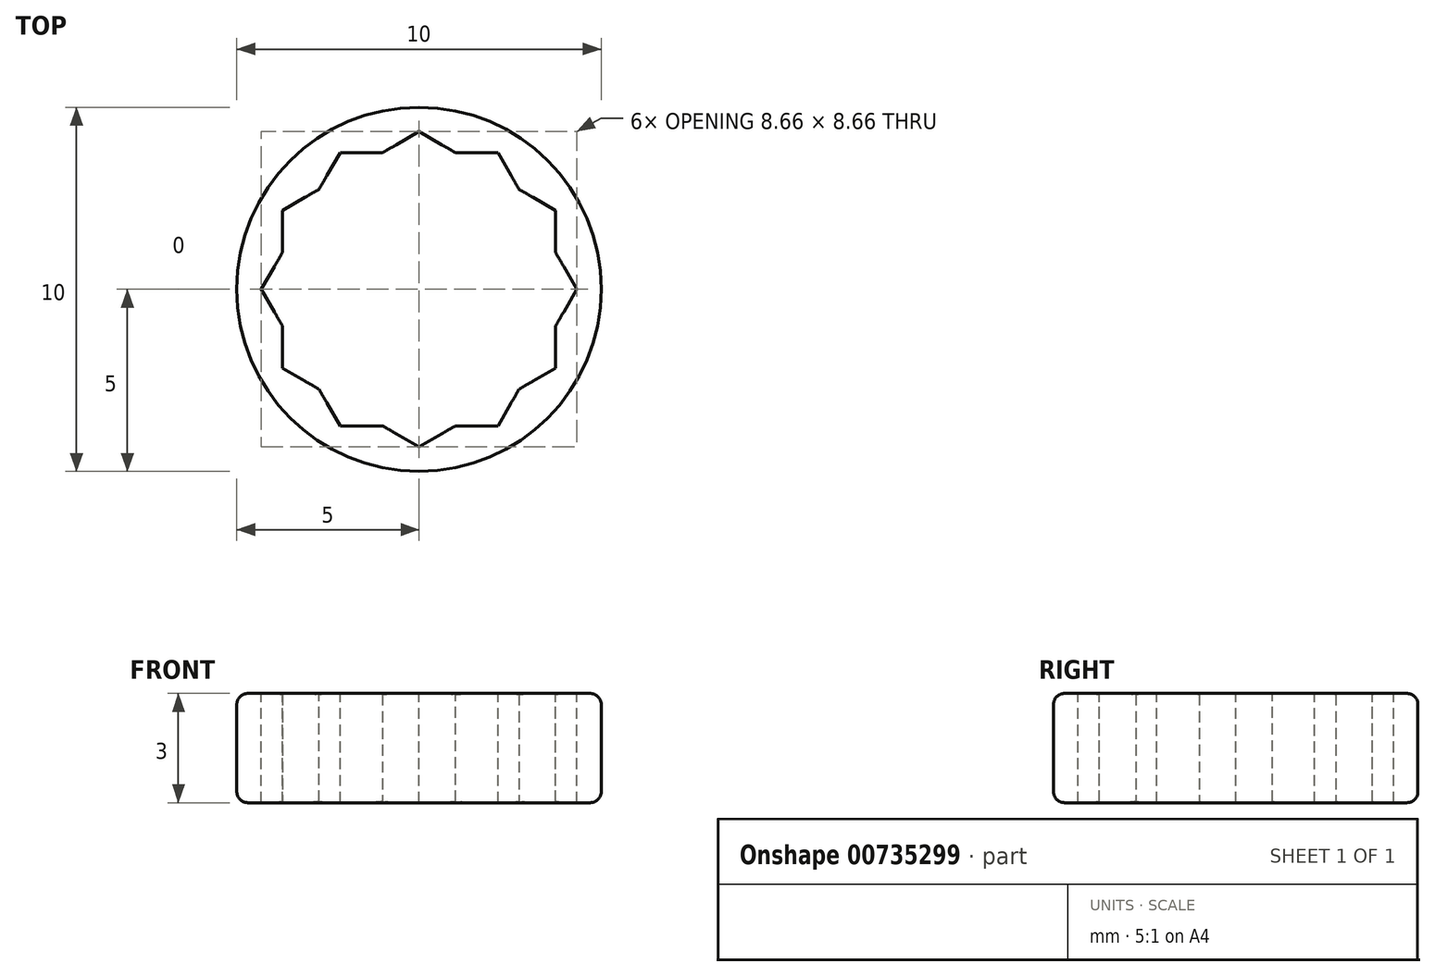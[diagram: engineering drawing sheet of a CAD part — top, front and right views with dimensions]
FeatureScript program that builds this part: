
annotation { "Feature Type Name" : "Feature", "Feature Type Description" : "" }
export const myFeature = defineFeature(function(context is Context, id is Id, definition is map)
    precondition{}
    {
        {
            var Q0;
            Q0=qCreatedBy(makeId("Top.planeOp"),FACE);
            var sketch = newSketch(context, id + "F0", { "sketchPlane" : qUnion([Q0])});
            skCircle(sketch, "E0", {"center": v(0, 0) * mm, "radius": 5 * mm});
            skCircle(sketch, "E1", {"center": v(0, 0) * mm, "radius": 3.72 * mm});
            skSolve(sketch);
        }
        {
            var Q0;
            Q0=makeQuery(id+"F0.imprint","IMPRINT",FACE,{"disambiguationData":[TD([[makeQuery(id+"F0.imprint","IMPRINT",EDGE,{"derivedFrom":sQuery(id+"F0.wireOp",EDGE,"E0")}),1.0]])]});
            extrude(context, id + "F1", {"entities" : qUnion([Q0]), "depth" : 3 * mm, "offsetDistance" : 25 * mm});
        }
        {
            var Q0;
            Q0=makeQuery(id+"F1.opExtrude","CAP_EDGE",EDGE,{"disambiguationData":[OSD([sQuery(id+"F0.wireOp",EDGE,"E0")])],"isStart":false});
            var Q1;
            Q1=makeQuery(id+"F1.opExtrude","CAP_EDGE",EDGE,{"disambiguationData":[OSD([sQuery(id+"F0.wireOp",EDGE,"E1")])],"isStart":false});
            var Q2;
            Q2=makeQuery(id+"F1.opExtrude","CAP_EDGE",EDGE,{"disambiguationData":[OSD([sQuery(id+"F0.wireOp",EDGE,"E0")])],"isStart":true});
            var Q3;
            Q3=makeQuery(id+"F1.opExtrude","CAP_EDGE",EDGE,{"disambiguationData":[OSD([sQuery(id+"F0.wireOp",EDGE,"E1")])],"isStart":true});
            fillet(context, id + "F2", {"entities" : qUnion([Q0, Q1, Q2, Q3]), "radius" : 0.3 * mm, "tangentPropagation" : true, "allowEdgeOverflow" : false});
        }
        {
            var Q0;
            Q0=qCreatedBy(makeId("Top.planeOp"),FACE);
            var sketch = newSketch(context, id + "F3", { "sketchPlane" : qUnion([Q0])});
            skCircle(sketch, "E2.cCircle", {"center": v(0, 0) * mm, "radius": 3.75 * mm, "construction": true});
            skLineSegment(sketch, "E2.0", {"start": v(3.75, 2.17) * mm, "end": v(3.75, -2.17) * mm});
            skLineSegment(sketch, "E2.1", {"start": v(3.75, -2.17) * mm, "end": v(0, -4.33) * mm});
            skLineSegment(sketch, "E2.2", {"start": v(0, -4.33) * mm, "end": v(-3.75, -2.17) * mm});
            skLineSegment(sketch, "E2.3", {"start": v(-3.75, -2.17) * mm, "end": v(-3.75, 2.17) * mm});
            skLineSegment(sketch, "E2.4", {"start": v(-3.75, 2.17) * mm, "end": v(0, 4.33) * mm});
            skLineSegment(sketch, "E2.5", {"start": v(0, 4.33) * mm, "end": v(3.75, 2.17) * mm});
            skPoint(sketch, "E2.0.midPoint", {"position": v(3.75, 0) * mm});
            skSolve(sketch);
        }
        {
            var Q0;
            Q0 = qSketchRegion(id + "F3", true);
            extrude(context, id + "F4", {"entities" : qUnion([Q0]), "operationType" : NewBodyOperationType.REMOVE, "oppositeDirection" : true, "depth" : 25 * mm, "offsetDistance" : 25 * mm, "symmetric" : true});
        }
        {
            var Q0;
            Q0=qCreatedBy(makeId("Top.planeOp"),FACE);
            var sketch = newSketch(context, id + "F5", { "sketchPlane" : qUnion([Q0])});
            skCircle(sketch, "E3.cCircle", {"center": v(0, 0) * mm, "radius": 3.75 * mm, "construction": true});
            skLineSegment(sketch, "E3.0", {"start": v(2.17, 3.75) * mm, "end": v(4.33, 0) * mm});
            skLineSegment(sketch, "E3.1", {"start": v(4.33, 0) * mm, "end": v(2.17, -3.75) * mm});
            skLineSegment(sketch, "E3.2", {"start": v(2.17, -3.75) * mm, "end": v(-2.17, -3.75) * mm});
            skLineSegment(sketch, "E3.3", {"start": v(-2.17, -3.75) * mm, "end": v(-4.33, 0) * mm});
            skLineSegment(sketch, "E3.4", {"start": v(-4.33, 0) * mm, "end": v(-2.17, 3.75) * mm});
            skLineSegment(sketch, "E3.5", {"start": v(-2.17, 3.75) * mm, "end": v(2.17, 3.75) * mm});
            skPoint(sketch, "E3.0.midPoint", {"position": v(3.25, 1.87) * mm});
            skSolve(sketch);
        }
        {
            var Q0;
            Q0 = qSketchRegion(id + "F5", true);
            extrude(context, id + "F6", {"entities" : qUnion([Q0]), "operationType" : NewBodyOperationType.REMOVE, "oppositeDirection" : true, "depth" : 25 * mm, "offsetDistance" : 25 * mm, "symmetric" : true});
        }
    });
